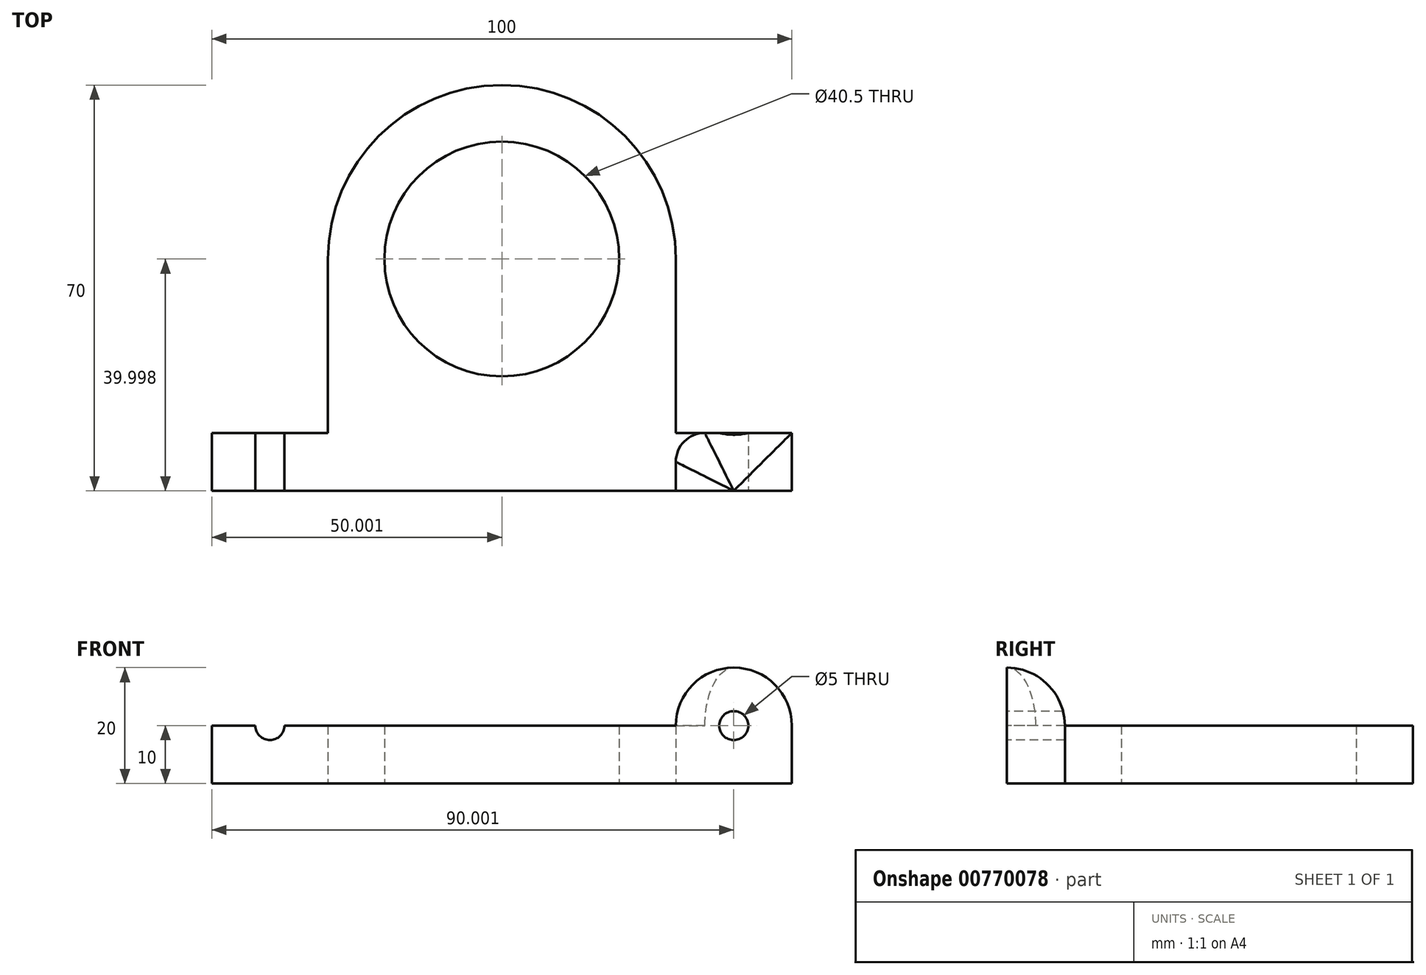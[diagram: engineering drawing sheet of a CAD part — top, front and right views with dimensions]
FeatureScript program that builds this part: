
annotation { "Feature Type Name" : "Feature", "Feature Type Description" : "" }
export const myFeature = defineFeature(function(context is Context, id is Id, definition is map)
    precondition{}
    {
        {
            var Q0;
            Q0=qCreatedBy(makeId("Top.planeOp"),FACE);
            var sketch = newSketch(context, id + "F0", { "sketchPlane" : qUnion([Q0])});
            skLineSegment(sketch, "E0.bottom", {"start": v(-60.5, 3.03) * mm, "end": v(-0.5, 3.03) * mm});
            skLineSegment(sketch, "E0.top", {"start": v(-60.5, -66.97) * mm, "end": v(-0.5, -66.97) * mm});
            skLineSegment(sketch, "E0.left", {"start": v(-60.5, 3.03) * mm, "end": v(-60.5, -66.97) * mm});
            skLineSegment(sketch, "E0.right", {"start": v(-0.5, 3.03) * mm, "end": v(-0.5, -66.97) * mm});
            skCircle(sketch, "E1", {"center": v(-30.5, -26.97) * mm, "radius": 20.25 * mm});
            skSolve(sketch);
        }
        {
            var Q0;
            Q0=makeQuery(id+"F0.imprint","IMPRINT",FACE,{"disambiguationData":[TD([[makeQuery(id+"F0.imprint","IMPRINT",EDGE,{"derivedFrom":sQuery(id+"F0.wireOp",EDGE,"E0.bottom")}),-1.0]])]});
            extrude(context, id + "F1", {"entities" : qUnion([Q0]), "depth" : 10 * mm, "offsetDistance" : 25 * mm});
        }
        {
            var Q0;
            Q0=makeQuery(id+"F1.opExtrude","SWEPT_FACE",FACE,{"disambiguationData":[OSD([sQuery(id+"F0.wireOp",EDGE,"E0.right")])]});
            var sketch = newSketch(context, id + "F2", { "sketchPlane" : qUnion([Q0])});
            skLineSegment(sketch, "E2.bottom", {"start": v(-66.97, 10) * mm, "end": v(-56.97, 10) * mm});
            skLineSegment(sketch, "E2.top", {"start": v(-66.97, 0) * mm, "end": v(-56.97, 0) * mm});
            skLineSegment(sketch, "E2.left", {"start": v(-66.97, 10) * mm, "end": v(-66.97, 0) * mm});
            skLineSegment(sketch, "E2.right", {"start": v(-56.97, 10) * mm, "end": v(-56.97, 0) * mm});
            skLineSegment(sketch, "E3.top", {"start": v(-66.97, 20) * mm, "end": v(-56.97, 20) * mm});
            skLineSegment(sketch, "E3.left", {"start": v(-66.97, 10) * mm, "end": v(-66.97, 20) * mm});
            skLineSegment(sketch, "E3.right", {"start": v(-56.97, 10) * mm, "end": v(-56.97, 20) * mm});
            skLineSegment(sketch, "E4.top", {"start": v(-66.97, -5) * mm, "end": v(-56.97, -5) * mm});
            skLineSegment(sketch, "E4.left", {"start": v(-66.97, 0) * mm, "end": v(-66.97, -5) * mm});
            skLineSegment(sketch, "E4.right", {"start": v(-56.97, 0) * mm, "end": v(-56.97, -5) * mm});
            skSolve(sketch);
        }
        {
            var Q0;
            Q0=makeQuery(id+"F2.imprint","IMPRINT",FACE,{"disambiguationData":[TD([[makeQuery(id+"F2.imprint","IMPRINT",EDGE,{"derivedFrom":sQuery(id+"F2.wireOp",EDGE,"E2.bottom")}),1.0]])]});
            var Q1;
            Q1=makeQuery(id+"F2.imprint","IMPRINT",FACE,{"disambiguationData":[TD([[makeQuery(id+"F2.imprint","IMPRINT",EDGE,{"derivedFrom":sQuery(id+"F2.wireOp",EDGE,"E2.left")}),1.0]])]});
            var Q2;
            Q2=makeQuery(id+"F2.imprint","IMPRINT",FACE,{"disambiguationData":[TD([[makeQuery(id+"F2.imprint","IMPRINT",EDGE,{"derivedFrom":sQuery(id+"F2.wireOp",EDGE,"E2.bottom")}),-1.0]])]});
            extrude(context, id + "F3", {"entities" : qUnion([Q0, Q1, Q2]), "operationType" : NewBodyOperationType.ADD, "depth" : 20 * mm, "offsetDistance" : 25 * mm});
        }
        {
            var Q0;
            Q0=makeQuery(id+"F1.opExtrude","SWEPT_FACE",FACE,{"disambiguationData":[OSD([sQuery(id+"F0.wireOp",EDGE,"E0.left")])]});
            var sketch = newSketch(context, id + "F4", { "sketchPlane" : qUnion([Q0])});
            skLineSegment(sketch, "E5.bottom", {"start": v(66.97, 0) * mm, "end": v(56.97, 0) * mm});
            skLineSegment(sketch, "E5.top", {"start": v(66.97, 10) * mm, "end": v(56.97, 10) * mm});
            skLineSegment(sketch, "E5.left", {"start": v(66.97, 0) * mm, "end": v(66.97, 10) * mm});
            skLineSegment(sketch, "E5.right", {"start": v(56.97, 0) * mm, "end": v(56.97, 10) * mm});
            skLineSegment(sketch, "E6.top", {"start": v(66.97, -5) * mm, "end": v(56.97, -5) * mm});
            skLineSegment(sketch, "E6.left", {"start": v(66.97, 0) * mm, "end": v(66.97, -5) * mm});
            skLineSegment(sketch, "E6.right", {"start": v(56.97, 0) * mm, "end": v(56.97, -5) * mm});
            skLineSegment(sketch, "E7.top", {"start": v(66.97, 20) * mm, "end": v(56.97, 20) * mm});
            skLineSegment(sketch, "E7.left", {"start": v(66.97, 10) * mm, "end": v(66.97, 20) * mm});
            skLineSegment(sketch, "E7.right", {"start": v(56.97, 10) * mm, "end": v(56.97, 20) * mm});
            skSolve(sketch);
        }
        {
            var Q0;
            Q0=makeQuery(id+"F4.imprint","IMPRINT",FACE,{"disambiguationData":[TD([[makeQuery(id+"F4.imprint","IMPRINT",EDGE,{"derivedFrom":sQuery(id+"F4.wireOp",EDGE,"E5.bottom")}),1.0]])]});
            var Q1;
            Q1=makeQuery(id+"F4.imprint","IMPRINT",FACE,{"disambiguationData":[TD([[makeQuery(id+"F4.imprint","IMPRINT",EDGE,{"derivedFrom":sQuery(id+"F4.wireOp",EDGE,"E5.left")}),-1.0]])]});
            var Q2;
            Q2=makeQuery(id+"F4.imprint","IMPRINT",FACE,{"disambiguationData":[TD([[makeQuery(id+"F4.imprint","IMPRINT",EDGE,{"derivedFrom":sQuery(id+"F4.wireOp",EDGE,"E5.top")}),1.0]])]});
            extrude(context, id + "F5", {"entities" : qUnion([Q0, Q1, Q2]), "operationType" : NewBodyOperationType.ADD, "depth" : 20 * mm, "offsetDistance" : 25 * mm});
        }
        {
            var Q0;
            Q0=makeQuery(id+"F5.boolean.opBoolean","MERGE",FACE,{"derivedFrom":[makeQuery(id+"F3.boolean.opBoolean","MERGE",FACE,{"derivedFrom":[makeQuery(id+"F1.opExtrude","SWEPT_FACE",FACE,{"disambiguationData":[OSD([sQuery(id+"F0.wireOp",EDGE,"E0.top")])]}),makeQuery(id+"F3.opExtrude","SWEPT_FACE",FACE,{"disambiguationData":[OSD([sQuery(id+"F2.wireOp",EDGE,"E2.left")])]})]}),makeQuery(id+"F5.opExtrude","SWEPT_FACE",FACE,{"disambiguationData":[OSD([sQuery(id+"F4.wireOp",EDGE,"E5.left")])]})]});
            var sketch = newSketch(context, id + "F6", { "sketchPlane" : qUnion([Q0])});
            skCircle(sketch, "E8", {"center": v(-70.5, 10) * mm, "radius": 2.5 * mm});
            skCircle(sketch, "E9", {"center": v(9.5, 10) * mm, "radius": 2.5 * mm});
            skSolve(sketch);
        }
        {
            var Q0;
            Q0=makeQuery(id+"F6.imprint","IMPRINT",FACE,{"disambiguationData":[TD([[makeQuery(id+"F6.imprint","IMPRINT",EDGE,{"derivedFrom":sQuery(id+"F6.wireOp",EDGE,"E8")}),1.0]])]});
            var Q1;
            Q1=makeQuery(id+"F6.imprint","IMPRINT",FACE,{"disambiguationData":[TD([[makeQuery(id+"F6.imprint","IMPRINT",EDGE,{"derivedFrom":sQuery(id+"F6.wireOp",EDGE,"E9")}),1.0]])]});
            extrude(context, id + "F7", {"entities" : qUnion([Q0, Q1]), "operationType" : NewBodyOperationType.REMOVE, "oppositeDirection" : true, "depth" : 25 * mm, "offsetDistance" : 25 * mm});
        }
        {
            var Q0;
            {var subQ0=sQuery(id+"F4.wireOp",EDGE,"E7.right");var subQ1=sQuery(id+"F4.wireOp",EDGE,"E6.right");var subQ2=sQuery(id+"F4.wireOp",EDGE,"E5.right");Q0=makeQuery(id+"F5.boolean.opBoolean","SPLIT",EDGE,{"disambiguationData":[topologyDisambiguationEdgeConnected([makeQuery(id+"F1.opExtrude","SWEPT_FACE",FACE,{"disambiguationData":[OSD([sQuery(id+"F0.wireOp",EDGE,"E0.left")])]}),makeQuery(id+"F5.opExtrude","SWEPT_FACE",FACE,{"disambiguationData":[OSD([subQ2,subQ1,subQ0])]})])],"derivedFrom":makeQuery(id+"F5.opExtrude","CAP_EDGE",EDGE,{"disambiguationData":[OSD([subQ2,subQ1,subQ0])],"isStart":true})});}
            var Q1;
            {var subQ0=sQuery(id+"F2.wireOp",EDGE,"E4.right");var subQ1=sQuery(id+"F2.wireOp",EDGE,"E3.right");var subQ2=sQuery(id+"F2.wireOp",EDGE,"E2.right");Q1=makeQuery(id+"F3.boolean.opBoolean","SPLIT",EDGE,{"disambiguationData":[topologyDisambiguationEdgeConnected([makeQuery(id+"F1.opExtrude","SWEPT_FACE",FACE,{"disambiguationData":[OSD([sQuery(id+"F0.wireOp",EDGE,"E0.right")])]}),makeQuery(id+"F3.opExtrude","SWEPT_FACE",FACE,{"disambiguationData":[OSD([subQ2,subQ1,subQ0])]})])],"derivedFrom":makeQuery(id+"F3.opExtrude","CAP_EDGE",EDGE,{"disambiguationData":[OSD([subQ2,subQ1,subQ0])],"isStart":true})});}
            fillet(context, id + "F8", {"entities" : qUnion([Q0, Q1]), "radius" : 5 * mm, "tangentPropagation" : true, "allowEdgeOverflow" : false});
        }
        {
            var Q0;
            Q0=makeQuery(id+"F1.opExtrude","SWEPT_EDGE",EDGE,{"disambiguationData":[OSD([sQuery(id+"F0.wireOp",EDGE,"E0.bottom"),sQuery(id+"F0.wireOp",EDGE,"E0.left")])]});
            var Q1;
            Q1=makeQuery(id+"F1.opExtrude","SWEPT_EDGE",EDGE,{"disambiguationData":[OSD([sQuery(id+"F0.wireOp",EDGE,"E0.bottom"),sQuery(id+"F0.wireOp",EDGE,"E0.right")])]});
            fillet(context, id + "F9", {"entities" : qUnion([Q0, Q1]), "radius" : 30 * mm, "tangentPropagation" : true, "allowEdgeOverflow" : false});
        }
        {
            var Q0;
            Q0=makeQuery(id+"F3.opExtrude","CAP_EDGE",EDGE,{"disambiguationData":[OSD([sQuery(id+"F2.wireOp",EDGE,"E4.top")])],"isStart":false});
            var Q1;
            Q1=makeQuery(id+"F3.opExtrude","CAP_EDGE",EDGE,{"disambiguationData":[OSD([sQuery(id+"F2.wireOp",EDGE,"E3.top")])],"isStart":false});
            var Q2;
            Q2=makeQuery(id+"F5.opExtrude","CAP_EDGE",EDGE,{"disambiguationData":[OSD([sQuery(id+"F4.wireOp",EDGE,"E6.top")])],"isStart":false});
            var Q3;
            Q3=makeQuery(id+"F5.opExtrude","CAP_EDGE",EDGE,{"disambiguationData":[OSD([sQuery(id+"F4.wireOp",EDGE,"E7.top")])],"isStart":false});
            var Q4;
            Q4=makeQuery(id+"F5.opExtrude","CAP_EDGE",EDGE,{"disambiguationData":[OSD([sQuery(id+"F4.wireOp",EDGE,"E7.top")])],"isStart":true});
            var Q5;
            Q5=makeQuery(id+"F3.opExtrude","CAP_EDGE",EDGE,{"disambiguationData":[OSD([sQuery(id+"F2.wireOp",EDGE,"E3.top")])],"isStart":true});
            fillet(context, id + "F10", {"entities" : qUnion([Q0, Q1, Q2, Q3, Q4, Q5]), "radius" : 10 * mm, "tangentPropagation" : true, "allowEdgeOverflow" : false});
        }
    });
